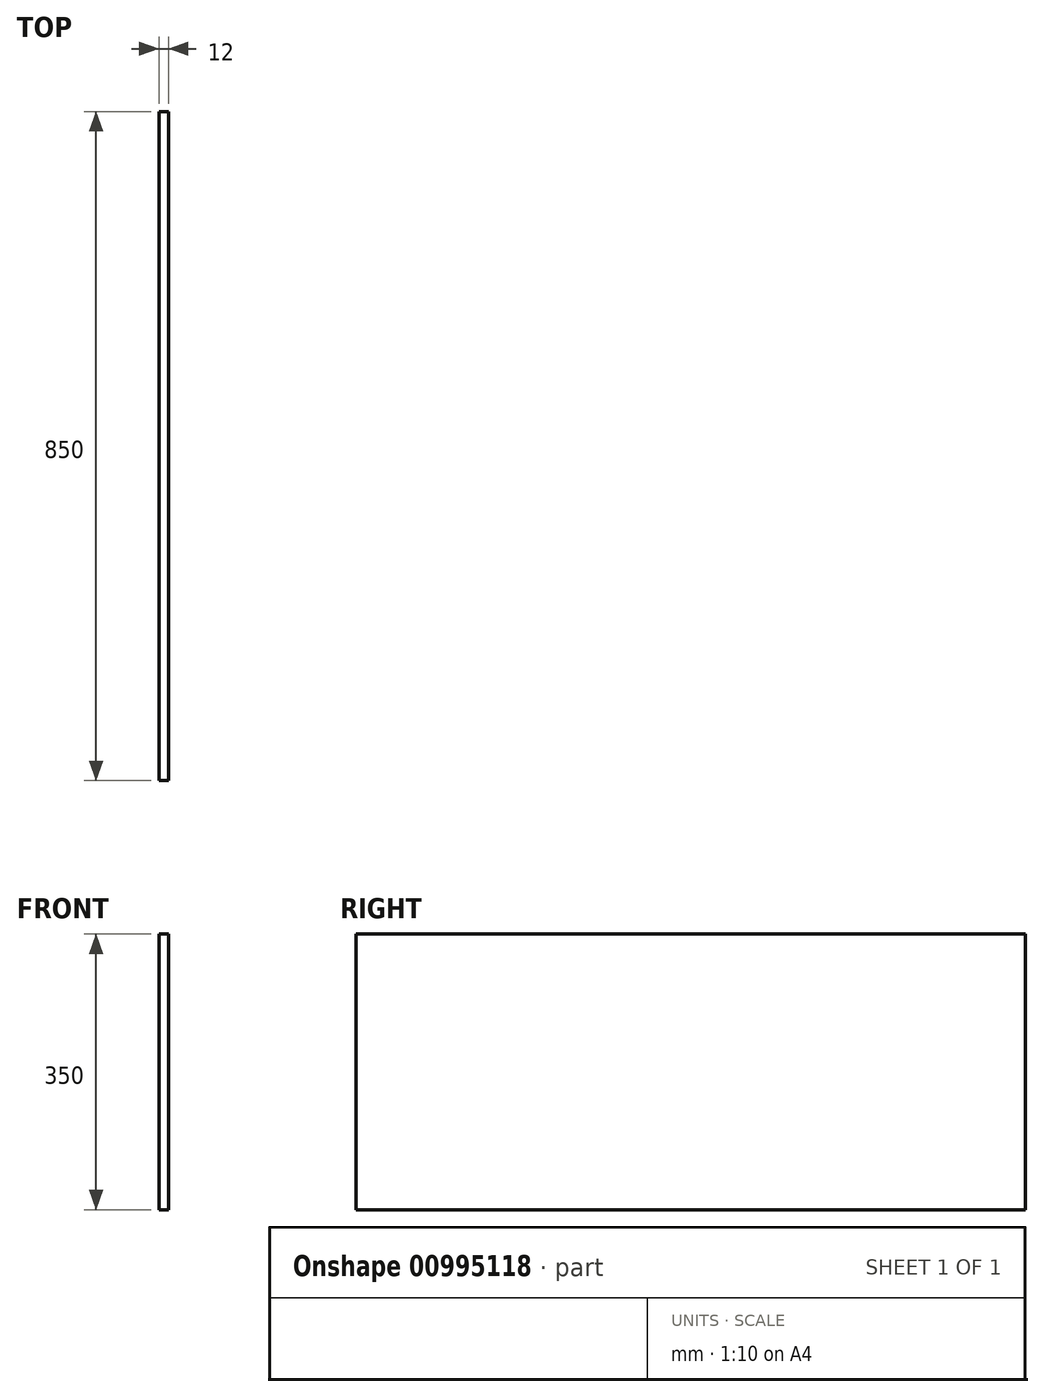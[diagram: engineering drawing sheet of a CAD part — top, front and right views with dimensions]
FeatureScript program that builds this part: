
annotation { "Feature Type Name" : "Feature", "Feature Type Description" : "" }
export const myFeature = defineFeature(function(context is Context, id is Id, definition is map)
    precondition{}
    {
        {
            var Q0;
            Q0=qCreatedBy(makeId("Front.planeOp"),FACE);
            var sketch = newSketch(context, id + "F0", { "sketchPlane" : qUnion([Q0])});
            skLineSegment(sketch, "E0.bottom", {"start": v(-6, 350) * mm, "end": v(6, 350) * mm});
            skLineSegment(sketch, "E0.top", {"start": v(-6, 0) * mm, "end": v(6, 0) * mm});
            skLineSegment(sketch, "E0.left", {"start": v(-6, 350) * mm, "end": v(-6, 0) * mm});
            skLineSegment(sketch, "E0.right", {"start": v(6, 350) * mm, "end": v(6, 0) * mm});
            skSolve(sketch);
        }
        {
            var Q0;
            Q0 = qSketchRegion(id + "F0", true);
            extrude(context, id + "F1", {"entities" : qUnion([Q0]), "oppositeDirection" : true, "depth" : 850 * mm, "offsetDistance" : 25 * mm});
        }
    });
